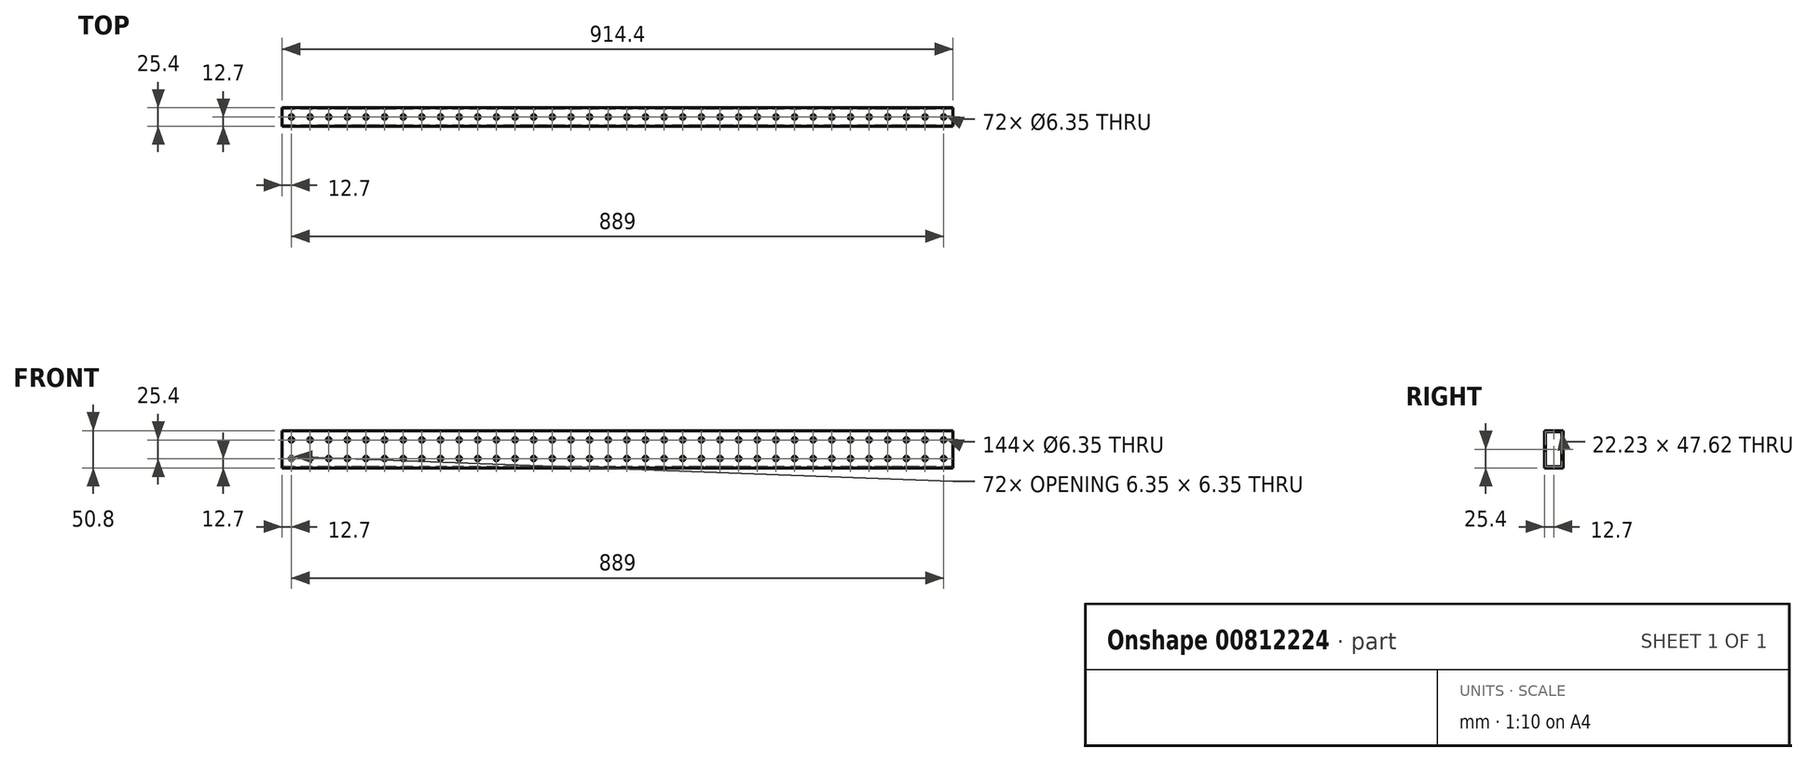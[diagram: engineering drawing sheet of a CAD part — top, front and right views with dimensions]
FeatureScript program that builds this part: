
annotation { "Feature Type Name" : "Feature", "Feature Type Description" : "" }
export const myFeature = defineFeature(function(context is Context, id is Id, definition is map)
    precondition{}
    {
        {
            var Q0;
            Q0=qCreatedBy(makeId("Right.planeOp"),FACE);
            var sketch = newSketch(context, id + "F0", { "sketchPlane" : qUnion([Q0])});
            skLineSegment(sketch, "E0.bottom", {"start": v(-12.7, 25.4) * mm, "end": v(12.7, 25.4) * mm});
            skLineSegment(sketch, "E0.top", {"start": v(-12.7, -25.4) * mm, "end": v(12.7, -25.4) * mm});
            skLineSegment(sketch, "E0.left", {"start": v(-12.7, 25.4) * mm, "end": v(-12.7, -25.4) * mm});
            skLineSegment(sketch, "E0.right", {"start": v(12.7, 25.4) * mm, "end": v(12.7, -25.4) * mm});
            skPoint(sketch, "E0.middle", {"position": v(0, 0) * mm});
            skLineSegment(sketch, "E1.0", {"start": v(-11.11, -23.81) * mm, "end": v(11.11, -23.81) * mm});
            skLineSegment(sketch, "E1.1", {"start": v(-11.11, 23.81) * mm, "end": v(-11.11, -23.81) * mm});
            skLineSegment(sketch, "E1.2", {"start": v(-11.11, 23.81) * mm, "end": v(11.11, 23.81) * mm});
            skLineSegment(sketch, "E1.3", {"start": v(11.11, 23.81) * mm, "end": v(11.11, -23.81) * mm});
            skSolve(sketch);
        }
        {
            var Q0;
            Q0=makeQuery(id+"F0.imprint","IMPRINT",FACE,{"disambiguationData":[TD([[makeQuery(id+"F0.imprint","IMPRINT",EDGE,{"derivedFrom":sQuery(id+"F0.wireOp",EDGE,"E0.bottom")}),-1.0]])]});
            extrude(context, id + "F1", {"entities" : qUnion([Q0]), "depth" : 914.4 * mm, "offsetDistance" : 25.4 * mm});
        }
        {
            var Q0;
            Q0=makeQuery(id+"F1.opExtrude","SWEPT_FACE",FACE,{"disambiguationData":[OSD([sQuery(id+"F0.wireOp",EDGE,"E0.bottom")])]});
            var sketch = newSketch(context, id + "F2", { "sketchPlane" : qUnion([Q0])});
            skCircle(sketch, "E2", {"center": v(12.7, 0) * mm, "radius": 3.18 * mm});
            skCircle(sketch, "E3.1.0.0", {"center": v(38.1, 0) * mm, "radius": 3.18 * mm});
            skCircle(sketch, "E3.2.0.0", {"center": v(63.5, 0) * mm, "radius": 3.18 * mm});
            skCircle(sketch, "E3.3.0.0", {"center": v(88.9, 0) * mm, "radius": 3.18 * mm});
            skCircle(sketch, "E3.4.0.0", {"center": v(114.3, 0) * mm, "radius": 3.18 * mm});
            skCircle(sketch, "E3.5.0.0", {"center": v(139.7, 0) * mm, "radius": 3.18 * mm});
            skCircle(sketch, "E3.6.0.0", {"center": v(165.1, 0) * mm, "radius": 3.18 * mm});
            skCircle(sketch, "E3.7.0.0", {"center": v(190.5, 0) * mm, "radius": 3.18 * mm});
            skCircle(sketch, "E3.8.0.0", {"center": v(215.9, 0) * mm, "radius": 3.18 * mm});
            skCircle(sketch, "E3.9.0.0", {"center": v(241.3, 0) * mm, "radius": 3.18 * mm});
            skCircle(sketch, "E3.10.0.0", {"center": v(266.7, 0) * mm, "radius": 3.18 * mm});
            skCircle(sketch, "E3.11.0.0", {"center": v(292.1, 0) * mm, "radius": 3.18 * mm});
            skCircle(sketch, "E3.12.0.0", {"center": v(317.5, 0) * mm, "radius": 3.18 * mm});
            skCircle(sketch, "E3.13.0.0", {"center": v(342.9, 0) * mm, "radius": 3.18 * mm});
            skCircle(sketch, "E3.14.0.0", {"center": v(368.3, 0) * mm, "radius": 3.18 * mm});
            skCircle(sketch, "E3.15.0.0", {"center": v(393.7, 0) * mm, "radius": 3.18 * mm});
            skCircle(sketch, "E3.16.0.0", {"center": v(419.1, 0) * mm, "radius": 3.18 * mm});
            skCircle(sketch, "E3.17.0.0", {"center": v(444.5, 0) * mm, "radius": 3.18 * mm});
            skCircle(sketch, "E3.18.0.0", {"center": v(469.9, 0) * mm, "radius": 3.18 * mm});
            skCircle(sketch, "E3.19.0.0", {"center": v(495.3, 0) * mm, "radius": 3.18 * mm});
            skCircle(sketch, "E3.20.0.0", {"center": v(520.7, 0) * mm, "radius": 3.18 * mm});
            skCircle(sketch, "E3.21.0.0", {"center": v(546.1, 0) * mm, "radius": 3.18 * mm});
            skCircle(sketch, "E3.22.0.0", {"center": v(571.5, 0) * mm, "radius": 3.18 * mm});
            skCircle(sketch, "E3.23.0.0", {"center": v(596.9, 0) * mm, "radius": 3.18 * mm});
            skCircle(sketch, "E3.24.0.0", {"center": v(622.3, 0) * mm, "radius": 3.18 * mm});
            skCircle(sketch, "E3.25.0.0", {"center": v(647.7, 0) * mm, "radius": 3.18 * mm});
            skCircle(sketch, "E3.26.0.0", {"center": v(673.1, 0) * mm, "radius": 3.18 * mm});
            skCircle(sketch, "E3.27.0.0", {"center": v(698.5, 0) * mm, "radius": 3.18 * mm});
            skCircle(sketch, "E3.28.0.0", {"center": v(723.9, 0) * mm, "radius": 3.18 * mm});
            skCircle(sketch, "E3.29.0.0", {"center": v(749.3, 0) * mm, "radius": 3.18 * mm});
            skCircle(sketch, "E3.30.0.0", {"center": v(774.7, 0) * mm, "radius": 3.18 * mm});
            skCircle(sketch, "E3.31.0.0", {"center": v(800.1, 0) * mm, "radius": 3.18 * mm});
            skCircle(sketch, "E3.32.0.0", {"center": v(825.5, 0) * mm, "radius": 3.18 * mm});
            skCircle(sketch, "E3.33.0.0", {"center": v(850.9, 0) * mm, "radius": 3.18 * mm});
            skCircle(sketch, "E3.34.0.0", {"center": v(876.3, 0) * mm, "radius": 3.18 * mm});
            skCircle(sketch, "E3.35.0.0", {"center": v(901.7, 0) * mm, "radius": 3.18 * mm});
            skLineSegment(sketch, "E3.direction1", {"start": v(12.7, 0) * mm, "end": v(38.1, 0) * mm, "construction": true});
            skSolve(sketch);
        }
        {
            var Q0;
            Q0=qSketchRegion(id+"F2",true);
            extrude(context, id + "F3", {"entities" : qUnion([Q0]), "operationType" : NewBodyOperationType.REMOVE, "endBound" : BoundingType.THROUGH_ALL, "oppositeDirection" : true, "depth" : 25.4 * mm, "offsetDistance" : 25.4 * mm});
        }
        {
            var Q0;
            Q0=makeQuery(id+"F1.opExtrude","SWEPT_FACE",FACE,{"disambiguationData":[OSD([sQuery(id+"F0.wireOp",EDGE,"E0.left")])]});
            var sketch = newSketch(context, id + "F4", { "sketchPlane" : qUnion([Q0])});
            skCircle(sketch, "E4", {"center": v(12.7, 12.7) * mm, "radius": 3.18 * mm});
            skCircle(sketch, "E5.0.1.0", {"center": v(12.7, -12.7) * mm, "radius": 3.18 * mm});
            skCircle(sketch, "E5.1.0.0", {"center": v(38.1, 12.7) * mm, "radius": 3.18 * mm});
            skCircle(sketch, "E5.1.1.0", {"center": v(38.1, -12.7) * mm, "radius": 3.18 * mm});
            skCircle(sketch, "E5.2.0.0", {"center": v(63.5, 12.7) * mm, "radius": 3.18 * mm});
            skCircle(sketch, "E5.2.1.0", {"center": v(63.5, -12.7) * mm, "radius": 3.18 * mm});
            skCircle(sketch, "E5.3.0.0", {"center": v(88.9, 12.7) * mm, "radius": 3.18 * mm});
            skCircle(sketch, "E5.3.1.0", {"center": v(88.9, -12.7) * mm, "radius": 3.18 * mm});
            skCircle(sketch, "E5.4.0.0", {"center": v(114.3, 12.7) * mm, "radius": 3.18 * mm});
            skCircle(sketch, "E5.4.1.0", {"center": v(114.3, -12.7) * mm, "radius": 3.18 * mm});
            skCircle(sketch, "E5.5.0.0", {"center": v(139.7, 12.7) * mm, "radius": 3.18 * mm});
            skCircle(sketch, "E5.5.1.0", {"center": v(139.7, -12.7) * mm, "radius": 3.18 * mm});
            skCircle(sketch, "E5.6.0.0", {"center": v(165.1, 12.7) * mm, "radius": 3.18 * mm});
            skCircle(sketch, "E5.6.1.0", {"center": v(165.1, -12.7) * mm, "radius": 3.18 * mm});
            skCircle(sketch, "E5.7.0.0", {"center": v(190.5, 12.7) * mm, "radius": 3.18 * mm});
            skCircle(sketch, "E5.7.1.0", {"center": v(190.5, -12.7) * mm, "radius": 3.18 * mm});
            skCircle(sketch, "E5.8.0.0", {"center": v(215.9, 12.7) * mm, "radius": 3.18 * mm});
            skCircle(sketch, "E5.8.1.0", {"center": v(215.9, -12.7) * mm, "radius": 3.18 * mm});
            skCircle(sketch, "E5.9.0.0", {"center": v(241.3, 12.7) * mm, "radius": 3.18 * mm});
            skCircle(sketch, "E5.9.1.0", {"center": v(241.3, -12.7) * mm, "radius": 3.18 * mm});
            skCircle(sketch, "E5.10.0.0", {"center": v(266.7, 12.7) * mm, "radius": 3.18 * mm});
            skCircle(sketch, "E5.10.1.0", {"center": v(266.7, -12.7) * mm, "radius": 3.18 * mm});
            skCircle(sketch, "E5.11.0.0", {"center": v(292.1, 12.7) * mm, "radius": 3.18 * mm});
            skCircle(sketch, "E5.11.1.0", {"center": v(292.1, -12.7) * mm, "radius": 3.18 * mm});
            skCircle(sketch, "E5.12.0.0", {"center": v(317.5, 12.7) * mm, "radius": 3.18 * mm});
            skCircle(sketch, "E5.12.1.0", {"center": v(317.5, -12.7) * mm, "radius": 3.18 * mm});
            skCircle(sketch, "E5.13.0.0", {"center": v(342.9, 12.7) * mm, "radius": 3.18 * mm});
            skCircle(sketch, "E5.13.1.0", {"center": v(342.9, -12.7) * mm, "radius": 3.18 * mm});
            skCircle(sketch, "E5.14.0.0", {"center": v(368.3, 12.7) * mm, "radius": 3.18 * mm});
            skCircle(sketch, "E5.14.1.0", {"center": v(368.3, -12.7) * mm, "radius": 3.18 * mm});
            skCircle(sketch, "E5.15.0.0", {"center": v(393.7, 12.7) * mm, "radius": 3.18 * mm});
            skCircle(sketch, "E5.15.1.0", {"center": v(393.7, -12.7) * mm, "radius": 3.18 * mm});
            skCircle(sketch, "E5.16.0.0", {"center": v(419.1, 12.7) * mm, "radius": 3.18 * mm});
            skCircle(sketch, "E5.16.1.0", {"center": v(419.1, -12.7) * mm, "radius": 3.18 * mm});
            skCircle(sketch, "E5.17.0.0", {"center": v(444.5, 12.7) * mm, "radius": 3.18 * mm});
            skCircle(sketch, "E5.17.1.0", {"center": v(444.5, -12.7) * mm, "radius": 3.18 * mm});
            skCircle(sketch, "E5.18.0.0", {"center": v(469.9, 12.7) * mm, "radius": 3.18 * mm});
            skCircle(sketch, "E5.18.1.0", {"center": v(469.9, -12.7) * mm, "radius": 3.18 * mm});
            skCircle(sketch, "E5.19.0.0", {"center": v(495.3, 12.7) * mm, "radius": 3.18 * mm});
            skCircle(sketch, "E5.19.1.0", {"center": v(495.3, -12.7) * mm, "radius": 3.18 * mm});
            skCircle(sketch, "E5.20.0.0", {"center": v(520.7, 12.7) * mm, "radius": 3.18 * mm});
            skCircle(sketch, "E5.20.1.0", {"center": v(520.7, -12.7) * mm, "radius": 3.18 * mm});
            skCircle(sketch, "E5.21.0.0", {"center": v(546.1, 12.7) * mm, "radius": 3.18 * mm});
            skCircle(sketch, "E5.21.1.0", {"center": v(546.1, -12.7) * mm, "radius": 3.18 * mm});
            skCircle(sketch, "E5.22.0.0", {"center": v(571.5, 12.7) * mm, "radius": 3.18 * mm});
            skCircle(sketch, "E5.22.1.0", {"center": v(571.5, -12.7) * mm, "radius": 3.18 * mm});
            skCircle(sketch, "E5.23.0.0", {"center": v(596.9, 12.7) * mm, "radius": 3.18 * mm});
            skCircle(sketch, "E5.23.1.0", {"center": v(596.9, -12.7) * mm, "radius": 3.18 * mm});
            skCircle(sketch, "E5.24.0.0", {"center": v(622.3, 12.7) * mm, "radius": 3.18 * mm});
            skCircle(sketch, "E5.24.1.0", {"center": v(622.3, -12.7) * mm, "radius": 3.18 * mm});
            skCircle(sketch, "E5.25.0.0", {"center": v(647.7, 12.7) * mm, "radius": 3.18 * mm});
            skCircle(sketch, "E5.25.1.0", {"center": v(647.7, -12.7) * mm, "radius": 3.18 * mm});
            skCircle(sketch, "E5.26.0.0", {"center": v(673.1, 12.7) * mm, "radius": 3.18 * mm});
            skCircle(sketch, "E5.26.1.0", {"center": v(673.1, -12.7) * mm, "radius": 3.18 * mm});
            skCircle(sketch, "E5.27.0.0", {"center": v(698.5, 12.7) * mm, "radius": 3.18 * mm});
            skCircle(sketch, "E5.27.1.0", {"center": v(698.5, -12.7) * mm, "radius": 3.18 * mm});
            skCircle(sketch, "E5.28.0.0", {"center": v(723.9, 12.7) * mm, "radius": 3.18 * mm});
            skCircle(sketch, "E5.28.1.0", {"center": v(723.9, -12.7) * mm, "radius": 3.18 * mm});
            skCircle(sketch, "E5.29.0.0", {"center": v(749.3, 12.7) * mm, "radius": 3.18 * mm});
            skCircle(sketch, "E5.29.1.0", {"center": v(749.3, -12.7) * mm, "radius": 3.18 * mm});
            skCircle(sketch, "E5.30.0.0", {"center": v(774.7, 12.7) * mm, "radius": 3.18 * mm});
            skCircle(sketch, "E5.30.1.0", {"center": v(774.7, -12.7) * mm, "radius": 3.18 * mm});
            skCircle(sketch, "E5.31.0.0", {"center": v(800.1, 12.7) * mm, "radius": 3.18 * mm});
            skCircle(sketch, "E5.31.1.0", {"center": v(800.1, -12.7) * mm, "radius": 3.18 * mm});
            skCircle(sketch, "E5.32.0.0", {"center": v(825.5, 12.7) * mm, "radius": 3.18 * mm});
            skCircle(sketch, "E5.32.1.0", {"center": v(825.5, -12.7) * mm, "radius": 3.18 * mm});
            skCircle(sketch, "E5.33.0.0", {"center": v(850.9, 12.7) * mm, "radius": 3.18 * mm});
            skCircle(sketch, "E5.33.1.0", {"center": v(850.9, -12.7) * mm, "radius": 3.18 * mm});
            skCircle(sketch, "E5.34.0.0", {"center": v(876.3, 12.7) * mm, "radius": 3.18 * mm});
            skCircle(sketch, "E5.34.1.0", {"center": v(876.3, -12.7) * mm, "radius": 3.18 * mm});
            skCircle(sketch, "E5.35.0.0", {"center": v(901.7, 12.7) * mm, "radius": 3.18 * mm});
            skCircle(sketch, "E5.35.1.0", {"center": v(901.7, -12.7) * mm, "radius": 3.18 * mm});
            skLineSegment(sketch, "E5.direction1", {"start": v(12.7, 12.7) * mm, "end": v(38.1, 12.7) * mm, "construction": true});
            skLineSegment(sketch, "E5.direction2", {"start": v(12.7, 12.7) * mm, "end": v(12.7, -12.7) * mm, "construction": true});
            skSolve(sketch);
        }
        {
            var Q0;
            Q0=qSketchRegion(id+"F4",true);
            extrude(context, id + "F5", {"entities" : qUnion([Q0]), "operationType" : NewBodyOperationType.REMOVE, "oppositeDirection" : true, "depth" : 25.4 * mm, "offsetDistance" : 25.4 * mm});
        }
    });
